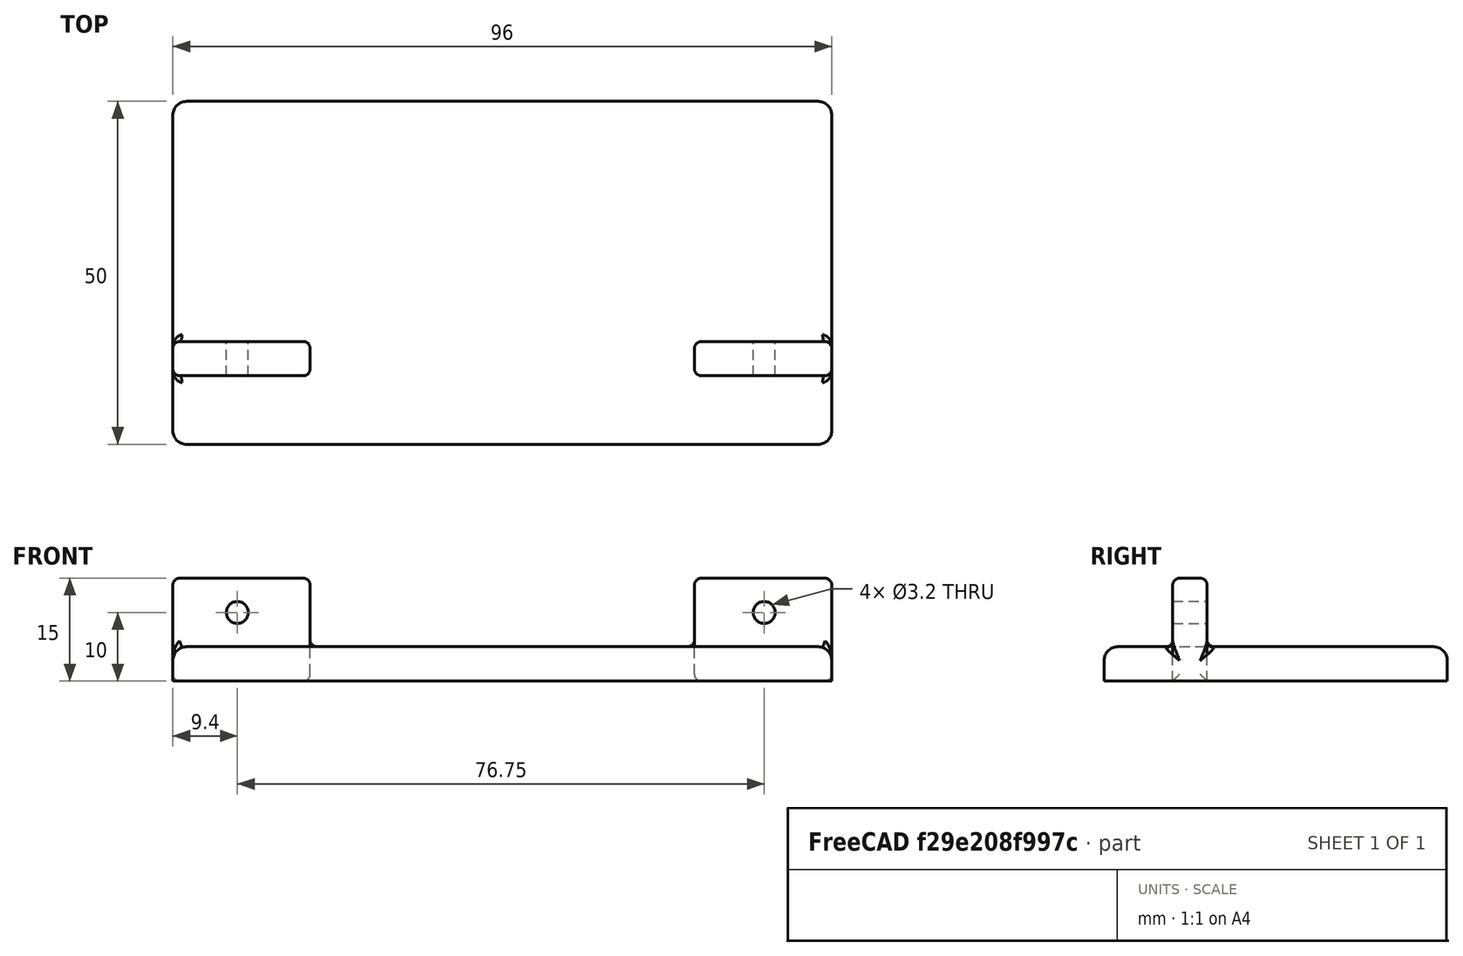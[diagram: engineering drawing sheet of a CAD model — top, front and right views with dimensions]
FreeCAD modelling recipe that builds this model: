
FCSTD DOCUMENT  (FreeCAD 1.0R39319 (Git))
Label: support-controle
License: All rights reserved
LicenseURL: https://en.wikipedia.org/wiki/All_rights_reserved
objects: PartDesign::Fillet×5, PartDesign::AdditiveBox×3, PartDesign::Body×3, PartDesign::AdditiveCylinder×2, PartDesign::Hole×2, PartDesign::Boolean×1
note: 41 computed .brp shape members not serialized (recipe doc carries the construction recipe); baked Part::Feature solids carry a one-line shape summary decoded from their .brp

FEATURE [PartDesign::AdditiveBox] Box
  AttacherType = Attacher::AttachEngine3D
  AttachmentOffset = pos=(-48,-10,0) rot=(0,0,1;0rad)
  AttachmentSupport = -> [X_Axis]
  Height = 5
  Length = 96
  MapMode = 2
  Placement = pos=(-48,-10,0) rot=(0,0,1;0rad)
  Refine = true
  Suppressed = false
  Width = 50
FEATURE [PartDesign::AdditiveBox] Box001
  AttacherType = Attacher::AttachEngine3D
  AttachmentOffset = pos=(0,10,-5) rot=(0,0,1;0rad)
  AttachmentSupport = -> [Box]
  Height = 15
  Length = 20
  MapMode = 5
  Placement = pos=(-48,0,0) rot=(0,0,1;0rad)
  Refine = true
  Suppressed = false
  Width = 5
FEATURE [PartDesign::AdditiveBox] Box002
  AttacherType = Attacher::AttachEngine3D
  AttachmentOffset = pos=(76,10,-5) rot=(0,0,1;0rad)
  AttachmentSupport = -> [Box]
  Height = 15
  Length = 20
  MapMode = 5
  Placement = pos=(28,0,0) rot=(0,0,1;0rad)
  Refine = true
  Suppressed = false
  Width = 5
FEATURE [PartDesign::AdditiveCylinder] Cylinder  label="Cylinder002"
  Angle = 360
  AttacherType = Attacher::AttachEngine3D
  AttachmentOffset = pos=(10.15,10,0) rot=(0,0,1;0rad)
  AttachmentSupport = -> [Box002]
  BaseFeature = -> Box002
  FirstAngle = 0
  Height = 10
  MapMode = 5
  Placement = pos=(38.15,2.2e-15,10) rot=(1,0,0;1.5708rad)
  Radius = 1.6
  Refine = true
  SecondAngle = 0
  Suppressed = false
FEATURE [PartDesign::AdditiveCylinder] Cylinder002  label="Cylinder001"
  Angle = 360
  AttacherType = Attacher::AttachEngine3D
  AttachmentOffset = pos=(9.4,10,0) rot=(0,0,1;0rad)
  AttachmentSupport = -> [Box001]
  BaseFeature = -> Box001
  FirstAngle = -5
  Height = 10
  MapMode = 5
  Placement = pos=(-38.6,2.2e-15,10) rot=(1,0,0;1.5708rad)
  Radius = 1.6
  Refine = true
  SecondAngle = 0
  Suppressed = false
FEATURE [PartDesign::Hole] Hole001
  BaseFeature = -> Cylinder002
  CustomThreadClearance = 0
  Depth = 25
  DepthType = 0
  Diameter = 3.2
  DrillForDepth = false
  DrillPoint = 1
  DrillPointAngle = 118
  HoleCutCountersinkAngle = 90
  HoleCutCustomValues = false
  HoleCutDepth = 0
  HoleCutDiameter = 6.1
  HoleCutType = 0
  ModelThread = false
  Placement = pos=(-38.6,2.2e-15,10) rot=(1,0,0;1.5708rad)
  Profile = -> Cylinder002 [Face2]
  Refine = true
  Suppressed = false
  Tapered = false
  TaperedAngle = 90
  ThreadClass = 0
  ThreadDepth = 25
  ThreadDepthType = 0
  ThreadDirection = 0
  ThreadFit = 0
  ThreadSize = 0
  ThreadType = 0
  Threaded = false
  UseCustomThreadClearance = false
FEATURE [PartDesign::Hole] Hole
  BaseFeature = -> Cylinder
  CustomThreadClearance = 0
  Depth = 25
  DepthType = 0
  Diameter = 3.2
  DrillForDepth = false
  DrillPoint = 1
  DrillPointAngle = 118
  HoleCutCountersinkAngle = 90
  HoleCutCustomValues = false
  HoleCutDepth = 0
  HoleCutDiameter = 6.1
  HoleCutType = 0
  ModelThread = false
  Placement = pos=(38.15,2.2e-15,10) rot=(1,0,0;1.5708rad)
  Profile = -> Cylinder [Face2]
  Refine = true
  Suppressed = false
  Tapered = false
  TaperedAngle = 90
  ThreadClass = 0
  ThreadDepth = 25
  ThreadDepthType = 0
  ThreadDirection = 0
  ThreadFit = 0
  ThreadSize = 0
  ThreadType = 0
  Threaded = false
  UseCustomThreadClearance = false
FEATURE [PartDesign::Fillet] Fillet
  Base = -> Hole001 [Face6,Face3,Face1]
  BaseFeature = -> Hole001
  Placement = pos=(-38.6,2.2e-15,10) rot=(1,0,0;1.5708rad)
  Radius = 1
  Refine = true
  SupportTransform = false
  Suppressed = false
  UseAllEdges = false
FEATURE [PartDesign::Body] Body001
  AllowCompound = false
  Group = -> [Box001,Cylinder002,Hole001,Fillet]
  Origin = -> Origin001
  Tip = -> Fillet
FEATURE [PartDesign::Fillet] Fillet001
  Base = -> Hole [Face6,Face3,Face1]
  BaseFeature = -> Hole
  Placement = pos=(38.15,2.2e-15,10) rot=(1,0,0;1.5708rad)
  Radius = 1
  Refine = true
  SupportTransform = false
  Suppressed = false
  UseAllEdges = false
FEATURE [PartDesign::Body] Body002
  AllowCompound = false
  Group = -> [Box002,Cylinder,Hole,Fillet001]
  Origin = -> Origin002
  Tip = -> Fillet001
FEATURE [PartDesign::Fillet] Fillet002
  Base = -> Box [Edge10,Edge1,Edge2,Edge5,Edge6,Edge7,Edge12,Edge3]
  BaseFeature = -> Box
  Placement = pos=(-48,-10,0) rot=(0,0,1;0rad)
  Radius = 2
  Refine = true
  SupportTransform = false
  Suppressed = false
  UseAllEdges = false
FEATURE [PartDesign::Boolean] Boolean
  BaseFeature = -> Fillet002
  Group = -> [Body001,Body002]
  Refine = true
  Suppressed = false
  Type = 0
  UsePlacement = true
FEATURE [PartDesign::Fillet] Fillet003
  Base = -> Boolean [Edge25,Edge30,Edge29,Edge31,Edge32]
  BaseFeature = -> Boolean
  Radius = 1
  Refine = true
  SupportTransform = false
  Suppressed = false
  UseAllEdges = false
FEATURE [PartDesign::Fillet] Fillet004
  Base = -> Fillet003 [Edge11,Edge13,Edge15,Edge17,Edge19]
  BaseFeature = -> Fillet003
  Radius = 1
  Refine = true
  SupportTransform = false
  Suppressed = false
  UseAllEdges = false
FEATURE [PartDesign::Body] Body
  AllowCompound = false
  Group = -> [Box,Fillet002,Boolean,Fillet003,Fillet004]
  Origin = -> Origin
  Tip = -> Fillet004
